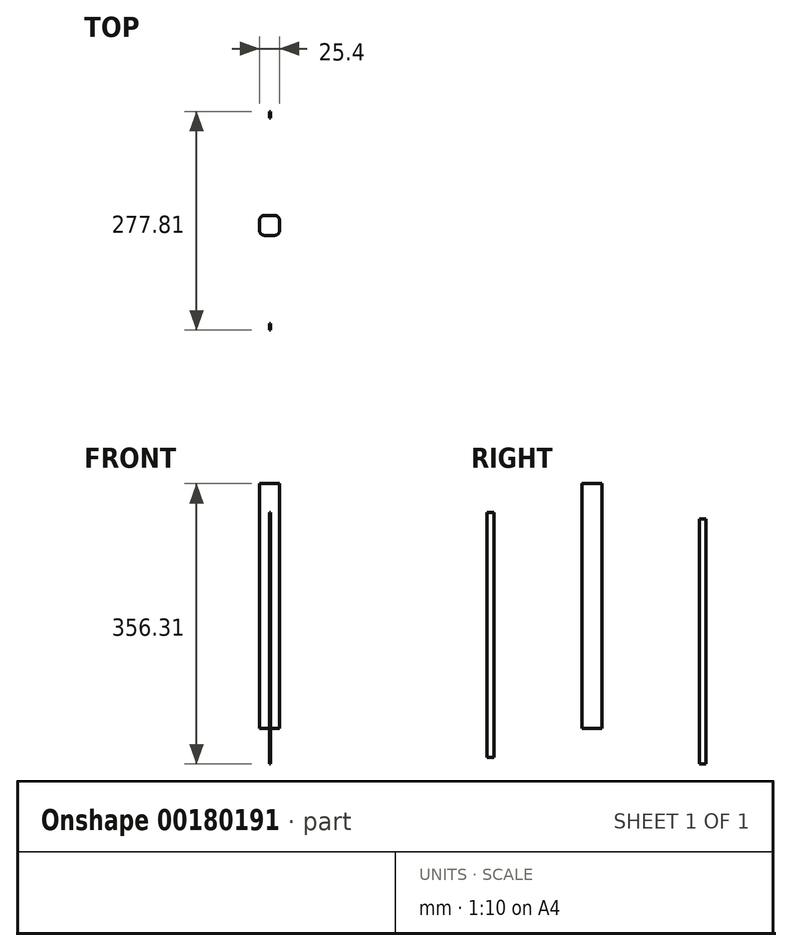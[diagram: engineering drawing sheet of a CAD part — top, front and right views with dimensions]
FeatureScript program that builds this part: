
annotation { "Feature Type Name" : "Feature", "Feature Type Description" : "" }
export const myFeature = defineFeature(function(context is Context, id is Id, definition is map)
    precondition{}
    {
        {
            var Q0;
            Q0=qCreatedBy(makeId("Top.planeOp"),FACE);
            var sketch = newSketch(context, id + "F0", { "sketchPlane" : qUnion([Q0])});
            skLineSegment(sketch, "E0.bottom", {"start": v(6.35, 12.7) * mm, "end": v(-6.35, 12.7) * mm});
            skLineSegment(sketch, "E0.top", {"start": v(6.35, -12.7) * mm, "end": v(-6.35, -12.7) * mm});
            skLineSegment(sketch, "E0.left", {"start": v(12.7, 6.35) * mm, "end": v(12.7, -6.35) * mm});
            skLineSegment(sketch, "E0.right", {"start": v(-12.7, 6.35) * mm, "end": v(-12.7, -6.35) * mm});
            skPoint(sketch, "E0.middle", {"position": v(0, 0) * mm});
            skPoint(sketch, "E1.visualSharp", {"position": v(-12.7, 12.7) * mm});
            skArc(sketch, "E1.filletArc", {"start": v(-6.35, 12.7) * mm, "mid": v(-10.84, 10.84) * mm, "end": v(-12.7, 6.35) * mm});
            skPoint(sketch, "E2.visualSharp", {"position": v(-12.7, -12.7) * mm});
            skArc(sketch, "E2.filletArc", {"start": v(-12.7, -6.35) * mm, "mid": v(-10.84, -10.84) * mm, "end": v(-6.35, -12.7) * mm});
            skPoint(sketch, "E3.visualSharp", {"position": v(12.7, -12.7) * mm});
            skArc(sketch, "E3.filletArc", {"start": v(6.35, -12.7) * mm, "mid": v(10.84, -10.84) * mm, "end": v(12.7, -6.35) * mm});
            skPoint(sketch, "E4.visualSharp", {"position": v(12.7, 12.7) * mm});
            skArc(sketch, "E4.filletArc", {"start": v(12.7, 6.35) * mm, "mid": v(10.84, 10.84) * mm, "end": v(6.35, 12.7) * mm});
            skSolve(sketch);
        }
        {
            var Q0;
            Q0=qSketchRegion(id+"F0",true);
            extrude(context, id + "F1", {"entities" : qUnion([Q0]), "depth" : 311.15 * mm});
        }
        {
            var Q0;
            Q0=qCreatedBy(makeId("Right.planeOp"),FACE);
            var sketch = newSketch(context, id + "F2", { "sketchPlane" : qUnion([Q0])});
            skLineSegment(sketch, "E5.bottom", {"start": v(-133.08, 274.33) * mm, "end": v(-124.62, 274.33) * mm});
            skLineSegment(sketch, "E5.top", {"start": v(-133.08, -36.82) * mm, "end": v(-124.62, -36.82) * mm});
            skLineSegment(sketch, "E5.left", {"start": v(-133.08, 274.33) * mm, "end": v(-133.08, -36.82) * mm});
            skLineSegment(sketch, "E5.right", {"start": v(-124.62, 274.33) * mm, "end": v(-124.62, -36.82) * mm});
            skSolve(sketch);
        }
        {
            var Q0;
            Q0=makeQuery(id+"F2.imprint","IMPRINT",FACE,{"disambiguationData":[TD([[makeQuery(id+"F2.imprint","IMPRINT",EDGE,{"derivedFrom":sQuery(id+"F2.wireOp",EDGE,"E5.bottom")}),-1.0]])]});
            extrude(context, id + "F3", {"entities" : qUnion([Q0]), "depth" : 1.27 * mm});
        }
        {
            var Q0;
            Q0=qCreatedBy(makeId("Right.planeOp"),FACE);
            var sketch = newSketch(context, id + "F4", { "sketchPlane" : qUnion([Q0])});
            skLineSegment(sketch, "E6.bottom", {"start": v(136.27, 265.99) * mm, "end": v(144.73, 265.99) * mm});
            skLineSegment(sketch, "E6.top", {"start": v(136.27, -45.16) * mm, "end": v(144.73, -45.16) * mm});
            skLineSegment(sketch, "E6.left", {"start": v(136.27, 265.99) * mm, "end": v(136.27, -45.16) * mm});
            skLineSegment(sketch, "E6.right", {"start": v(144.73, 265.99) * mm, "end": v(144.73, -45.16) * mm});
            skSolve(sketch);
        }
        {
            var Q0;
            Q0=qSketchRegion(id+"F4",true);
            extrude(context, id + "F5", {"entities" : qUnion([Q0]), "depth" : 1.27 * mm});
        }
    });
